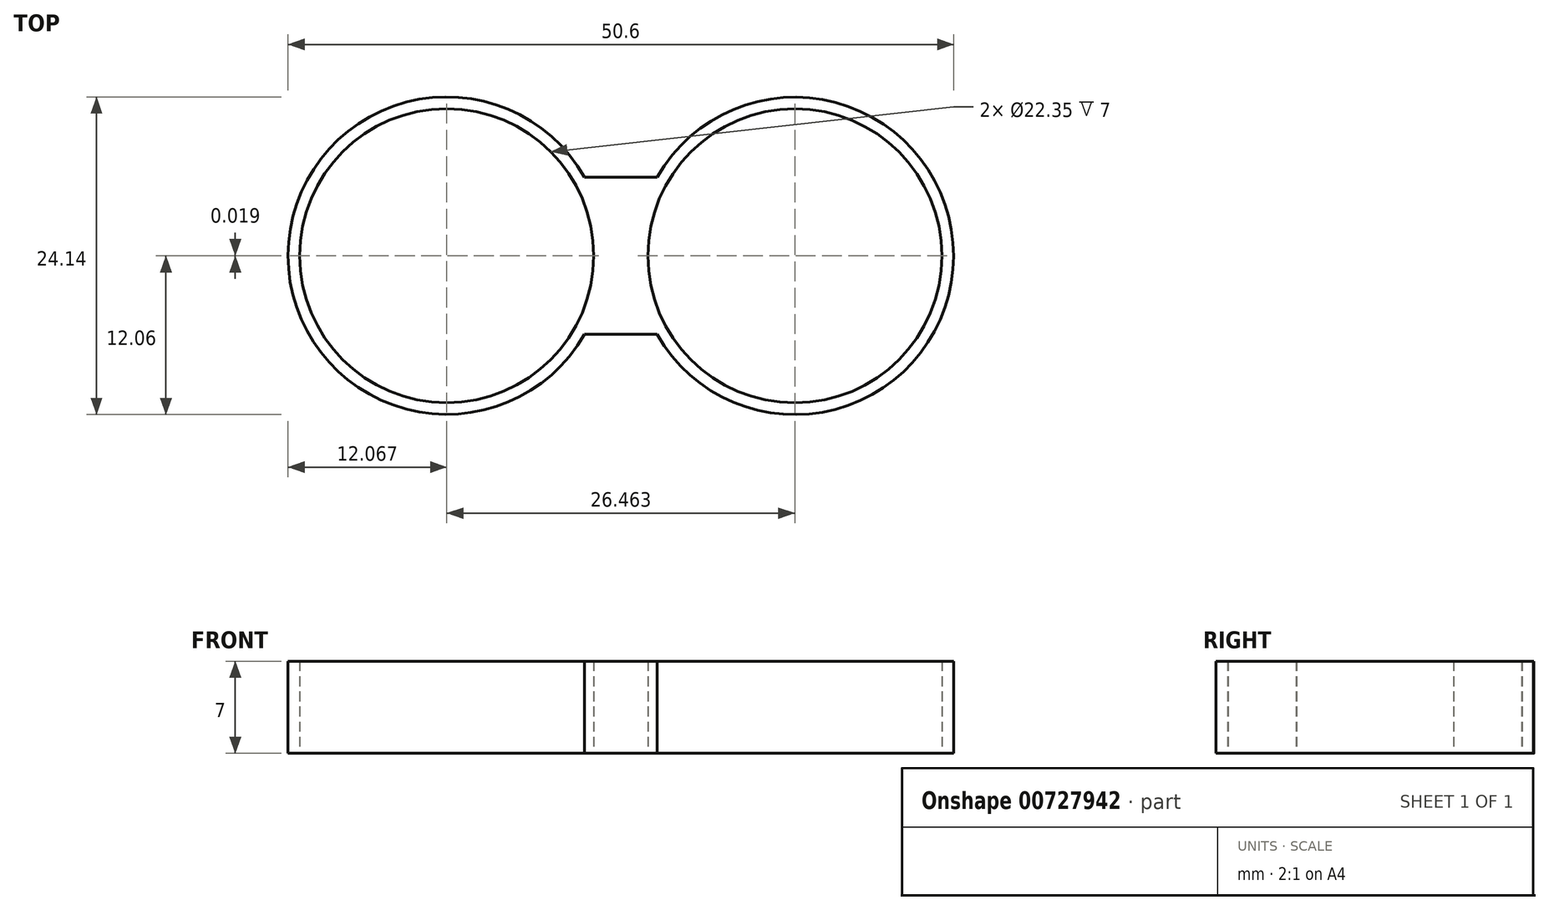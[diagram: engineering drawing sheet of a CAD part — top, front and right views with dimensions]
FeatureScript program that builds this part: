
annotation { "Feature Type Name" : "Feature", "Feature Type Description" : "" }
export const myFeature = defineFeature(function(context is Context, id is Id, definition is map)
    precondition{}
    {
        {
            var Q0;
            Q0=qCreatedBy(makeId("Top.planeOp"),FACE);
            var sketch = newSketch(context, id + "F0", { "sketchPlane" : qUnion([Q0])});
            skCircle(sketch, "E0", {"center": v(0, 0) * mm, "radius": 11.18 * mm});
            skCircle(sketch, "E1", {"center": v(-26.46, 0.02) * mm, "radius": 11.18 * mm});
            skCircle(sketch, "E2", {"center": v(-26.46, 0.02) * mm, "radius": 12.07 * mm});
            skCircle(sketch, "E3", {"center": v(0, 0) * mm, "radius": 12.07 * mm});
            skLineSegment(sketch, "E4", {"start": v(0, 0) * mm, "end": v(-26.46, 0.02) * mm});
            skLineSegment(sketch, "E5", {"start": v(-10.47, 5.99) * mm, "end": v(-15.98, 5.99) * mm});
            skLineSegment(sketch, "E6.MirrorCS", {"start": v(-10.48, -5.97) * mm, "end": v(-15.99, -5.97) * mm});
            skSolve(sketch);
        }
        {
            var Q0;
            Q0=makeQuery(id+"F0.imprint","IMPRINT",FACE,{"disambiguationData":[TD([[makeQuery(id+"F0.imprint","IMPRINT",EDGE,{"derivedFrom":sQuery(id+"F0.wireOp",EDGE,"E1")}),-1.0]])]});
            var Q1;
            {var subQ0=sQuery(id+"F0.wireOp",EDGE,"cNXRmXyi-zd3O-Q2zh-Z4gW-OQsMHLZz4ylj");var subQ1=sQuery(id+"F0.wireOp",EDGE,"E2");var subQ2=makeQuery(id+"F0.imprint","INTERSECT",VERTEX,{"derivedFrom":[subQ1,subQ0]});Q1=makeQuery(id+"F0.imprint","IMPRINT",FACE,{"disambiguationData":[TD([[makeQuery(id+"F0.imprint","IMPRINT",EDGE,{"disambiguationData":[TD([[subQ2,1.0]])],"derivedFrom":subQ1}),-1.0]])]});}
            var Q2;
            {var subQ0=sQuery(id+"F0.wireOp",EDGE,"362d6708-58a3-48f6-95f8-a93ba6fc152b0.MirrorCS");var subQ1=sQuery(id+"F0.wireOp",EDGE,"E2");var subQ2=makeQuery(id+"F0.imprint","INTERSECT",VERTEX,{"derivedFrom":[subQ1,subQ0]});Q2=makeQuery(id+"F0.imprint","IMPRINT",FACE,{"disambiguationData":[TD([[makeQuery(id+"F0.imprint","IMPRINT",EDGE,{"disambiguationData":[TD([[subQ2,-1.0]])],"derivedFrom":subQ1}),-1.0]])]});}
            var Q3;
            Q3=makeQuery(id+"F0.imprint","IMPRINT",FACE,{"disambiguationData":[TD([[makeQuery(id+"F0.imprint","IMPRINT",EDGE,{"derivedFrom":sQuery(id+"F0.wireOp",EDGE,"E0")}),-1.0]])]});
            extrude(context, id + "F1", {"entities" : qUnion([Q0, Q1, Q2, Q3]), "depth" : 7 * mm, "offsetDistance" : 25.4 * mm});
        }
    });
